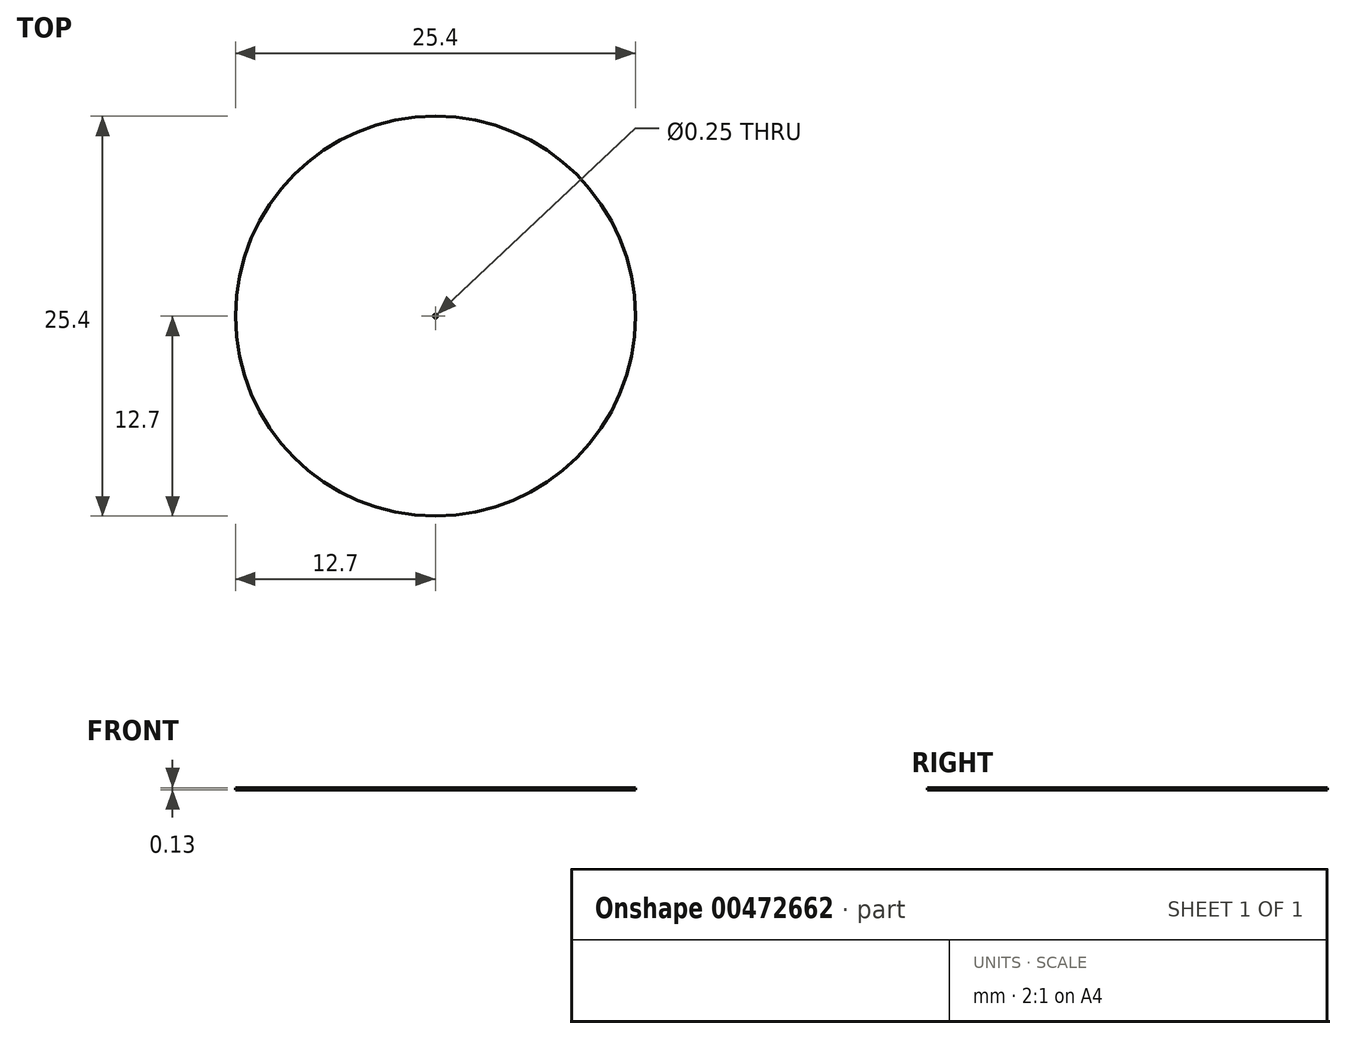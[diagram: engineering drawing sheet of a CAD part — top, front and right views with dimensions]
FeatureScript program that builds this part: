
annotation { "Feature Type Name" : "Feature", "Feature Type Description" : "" }
export const myFeature = defineFeature(function(context is Context, id is Id, definition is map)
    precondition{}
    {
        {
            assignVariable(context, id + "F0", {"name" : "ID", "anyValue" : 0.25});
        }
        {
            assignVariable(context, id + "F1", {"name" : "thickness", "anyValue" : 1 / 8});
        }
        {
            var Q0;
            Q0=qCreatedBy(makeId("Top.planeOp"),FACE);
            var sketch = newSketch(context, id + "F2", { "sketchPlane" : qUnion([Q0])});
            skCircle(sketch, "E0", {"center": v(0, 0) * mm, "radius": 12.7 * mm});
            skSolve(sketch);
        }
        {
            var Q0;
            Q0 = qSketchRegion(id + "F2", true);
            extrude(context, id + "F3", {"entities" : qUnion([Q0]), "depth" : (getVariable(context, 'thickness')) * mm});
        }
        {
            var Q0;
            Q0=sQuery(id+"F2.wireOp",VERTEX,"E0.center");
            var Q1;
            Q1=makeQuery(id+"F3.opExtrude","SWEPT_BODY",BODY,{"disambiguationData":[OSD([sQuery(id+"F2.wireOp",EDGE,"E0")])]});
            hole(context, id + "F4", {"style" : HoleStyle.SIMPLE, "endStyle" : HoleEndStyle.THROUGH, "oppositeDirection" : true, "holeDiameter" : (getVariable(context, 'ID')) * mm, "isTappedThrough" : true, "tappedDepth" : 12.7 * mm, "tapClearance" : 3, "startFromSketch" : true, "locations" : qUnion([Q0]), "scope" : qUnion([Q1])});
        }
    });
